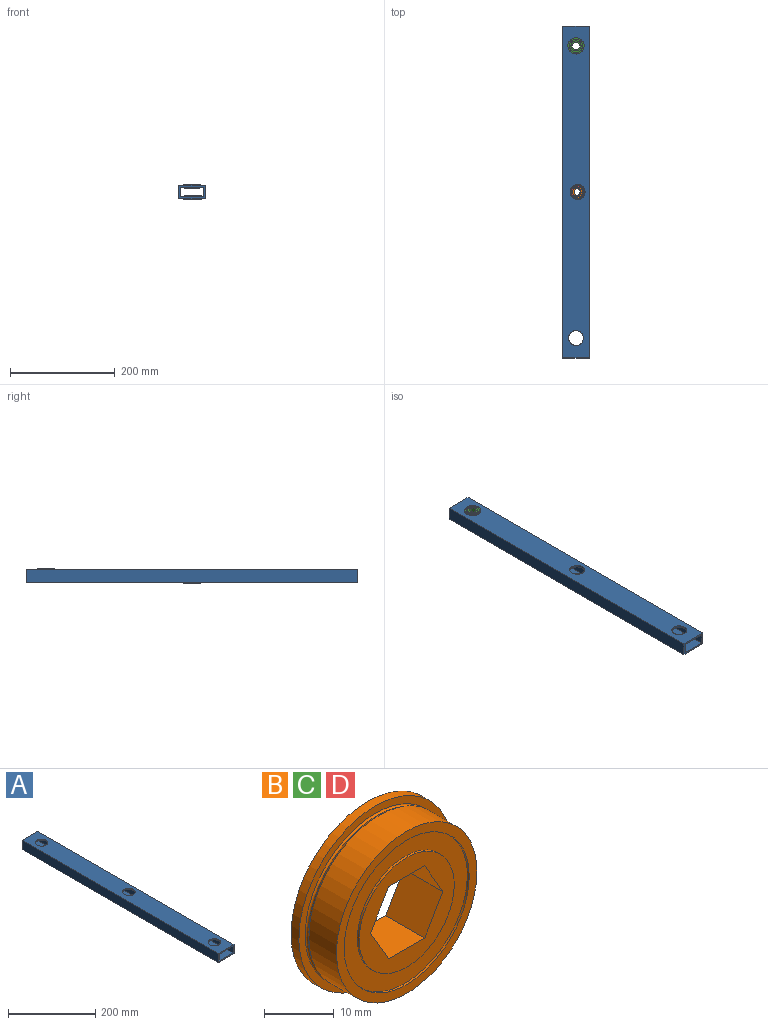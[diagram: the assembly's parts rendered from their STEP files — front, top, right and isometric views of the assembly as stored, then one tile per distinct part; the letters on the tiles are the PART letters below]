
ASSEMBLY  parts=4 mates=6
PART A: 16 faces, bbox 50.8x635x25.4 mm
  f0: plane 635x50.8mm, normal (0,0,-1), area 30334.1mm2, adj f1,f7,f8,f9,f13,f14,f15
  f1: plane 635x25.4mm, normal (1,0,0), area 16129mm2, adj f0,f2,f8,f9
  f2: plane 635x50.8mm, normal (0,0,1), area 30334.1mm2, adj f1,f7,f8,f9,f10,f11,f12
  f3: plane 635x44.45mm, normal (0,0,1), area 26301.8mm2, adj f4,f6,f8,f9,f13,f14,f15
  f4: plane 635x19.05mm, normal (1,0,0), area 12096.7mm2, adj f3,f5,f8,f9
  f5: plane 635x44.45mm, normal (0,0,-1), area 26301.8mm2, adj f4,f6,f8,f9,f10,f11,f12
  f6: plane 635x19.05mm, normal (-1,0,0), area 12096.8mm2, adj f3,f5,f8,f9
  f7: plane 635x25.4mm, normal (-1,0,0), area 16129mm2, adj f0,f2,f8,f9
  f8: plane 50.8x25.4mm, normal (0,-1,0), area 443.5mm2, adj f0,f1,f2,f3,f4,f5,f6,f7
  f9: plane 50.8x25.4mm, normal (0,1,0), area 443.5mm2, adj f0,f1,f2,f3,f4,f5,f6,f7
  f10: cylinder r=14.29mm len=28.58mm, axis (0,0,1), area 285mm2, adj f2,f5
  f11: cylinder r=14.29mm len=28.58mm, axis (0,0,1), area 285mm2, adj f2,f5
  f12: cylinder r=14.29mm len=28.58mm, axis (0,0,1), area 285mm2, adj f2,f5
  f13: cylinder r=14.29mm len=28.58mm, axis (0,0,1), area 285mm2, adj f0,f3
  f14: cylinder r=14.29mm len=28.58mm, axis (0,0,1), area 285mm2, adj f0,f3
  f15: cylinder r=14.29mm len=28.58mm, axis (0,0,1), area 285mm2, adj f0,f3
PART B: 21 faces, bbox 31.1x7.9x31.1 mm
  f0: torus R=14.27mm, axis (0,1,0), area 46.4mm2, adj f4,f10
  f1: cylinder r=9.65mm len=19.3mm, axis (0,1,0), area 23.1mm2, adj f12,f13
  f2: cylinder r=12.7mm len=25.4mm, axis (0,1,0), area 30.4mm2, adj f11,f12
  f3: cylinder r=14.27mm len=28.55mm, axis (0,1,0), area 502.3mm2, adj f4,f11
  f4: cone r=14.06mm half-angle=30deg, axis (0,-1,0), area 38.5mm2, adj f0,f3
  f5: cylinder r=15.56mm len=31.12mm, axis (0,1,0), area 155.2mm2, adj f9,f10
  f6: cylinder r=12.7mm len=25.4mm, axis (0,1,0), area 30.4mm2, adj f8,f9
  f7: cylinder r=9.65mm len=19.3mm, axis (0,1,0), area 23.1mm2, adj f8,f14
  f8: plane 25.4x25.4mm, normal (0,1,0), area 214mm2, adj f6,f7
  f9: plane 31.12x31.12mm, normal (0,1,0), area 253.7mm2, adj f5,f6
  f10: plane 31.12x31.12mm, normal (0,-1,0), area 120.2mm2, adj f0,f5
  f11: plane 28.55x28.55mm, normal (0,-1,0), area 133.5mm2, adj f2,f3
  f12: plane 25.4x25.4mm, normal (0,-1,0), area 214mm2, adj f1,f2
  f13: plane 19.3x19.3mm, normal (0,-1,0), area 152.6mm2, adj f1,f15,f16,f17,f18,f19,f20
  f14: plane 19.3x19.3mm, normal (0,1,0), area 152.6mm2, adj f7,f15,f16,f17,f18,f19,f20
  f15: plane 7.94x6.36mm, normal (-0.87,0,0.5), area 58.3mm2, adj f13,f14,f16,f20
  f16: plane 7.94x6.36mm, normal (-0.87,0,-0.5), area 58.3mm2, adj f13,f14,f15,f17
  f17: plane 7.94x7.34mm, normal (0,0,-1), area 58.3mm2, adj f13,f14,f16,f18
  f18: plane 7.94x6.36mm, normal (0.87,0,-0.5), area 58.3mm2, adj f13,f14,f17,f19
  f19: plane 7.94x6.36mm, normal (0.87,0,0.5), area 58.3mm2, adj f13,f14,f18,f20
  f20: plane 7.94x7.34mm, normal (0,0,1), area 58.3mm2, adj f13,f14,f15,f19
PART C: same geometry as B
PART D: same geometry as B
PLACE A t=(-26.98,-21.62,-11.32)mm fixed
PLACE B rot(axis=(-0.58,-0.58,0.58),120deg) t=(1.6,-339.12,-4.97)mm
PLACE C rot(axis=(1,0,0),90deg) t=(-1.58,-59.74,7.73)mm
PLACE D rot(axis=(-1,0,0),90deg) t=(-1.65,-339.12,-4.97)mm
MATE planar B.f0 <-> A.f0  axis (0,0,1) through (1.6,-339.12,-11.32)mm
MATE cylindrical C.f0 <-> A.f12  axis (0,0,1) through (-1.58,-59.74,13.33)mm
MATE cylindrical D.f0 <-> A.f10  axis (0,0,-1) through (-1.65,-339.12,-7.77)mm
MATE planar D.f0 <-> A.f0  axis (0,0,1) through (-1.65,-339.12,-11.32)mm
MATE cylindrical B.f0 <-> A.f11  axis (0,0,-1) through (1.6,-339.12,-7.77)mm
MATE planar C.f0 <-> A.f2  axis (0,0,-1) through (-1.58,-59.74,14.08)mm
